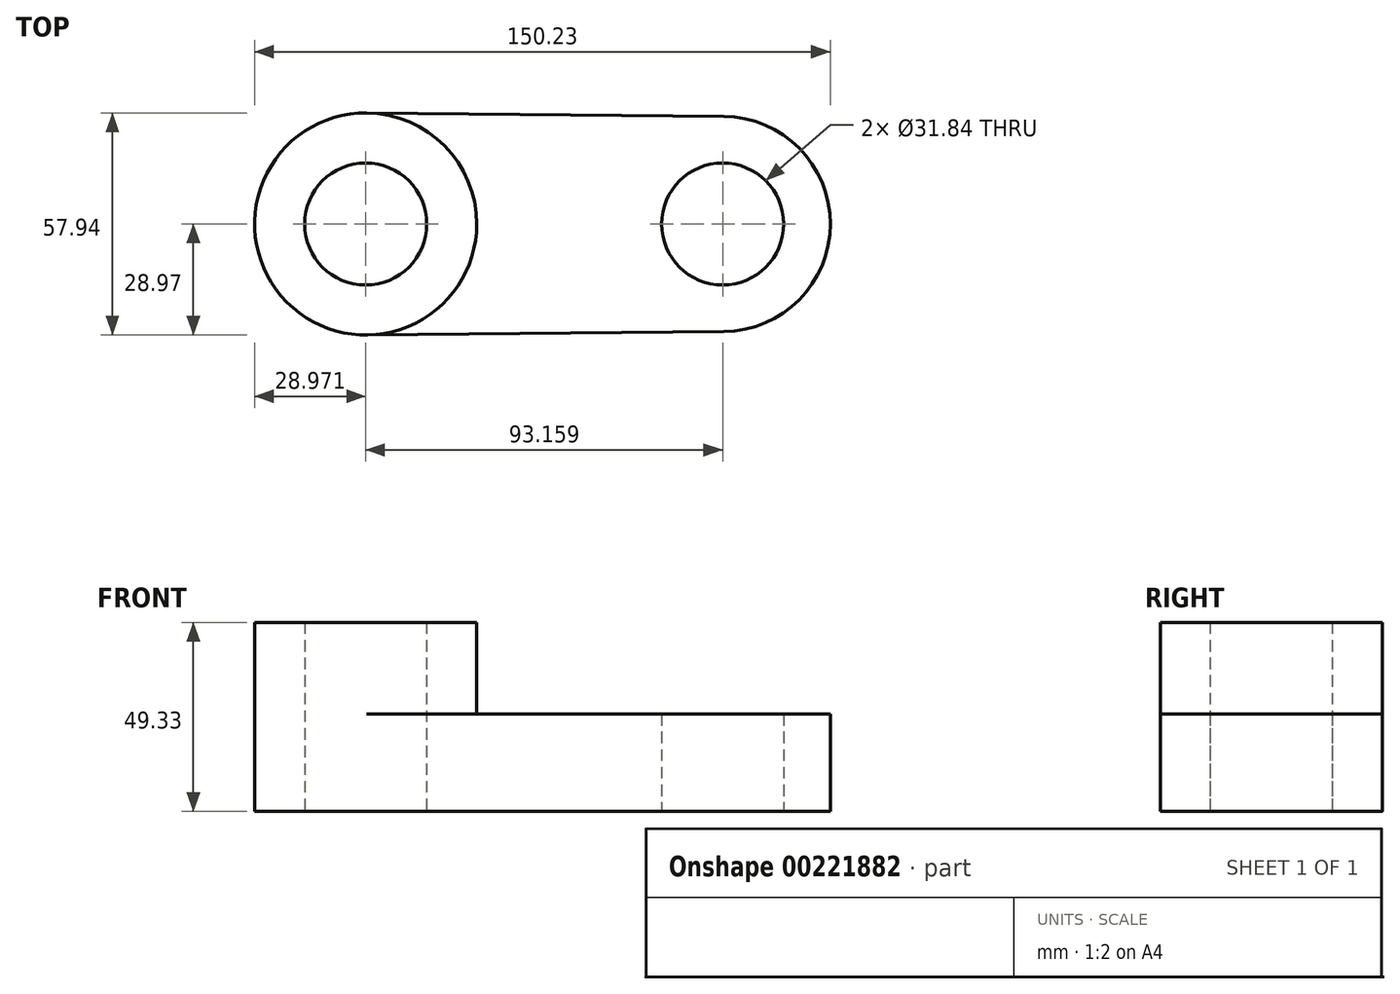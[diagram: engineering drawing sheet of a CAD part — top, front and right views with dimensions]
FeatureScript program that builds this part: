
annotation { "Feature Type Name" : "Feature", "Feature Type Description" : "" }
export const myFeature = defineFeature(function(context is Context, id is Id, definition is map)
    precondition{}
    {
        {
            var Q0;
            Q0=qCreatedBy(makeId("Top.planeOp"),FACE);
            var sketch = newSketch(context, id + "F0", { "sketchPlane" : qUnion([Q0])});
            skCircle(sketch, "E0", {"center": v(-46.58, 0) * mm, "radius": 15.92 * mm});
            skCircle(sketch, "E1", {"center": v(46.58, 0) * mm, "radius": 15.92 * mm});
            skArc(sketch, "E2", {"start": v(-46.3, 28.97) * mm, "mid": v(-75.55, 0) * mm, "end": v(-46.3, -28.97) * mm});
            skArc(sketch, "E3", {"start": v(46.84, -28.1) * mm, "mid": v(74.68, 0) * mm, "end": v(46.84, 28.1) * mm});
            skLineSegment(sketch, "E4", {"start": v(-46.3, 28.97) * mm, "end": v(46.84, 28.1) * mm});
            skLineSegment(sketch, "E5", {"start": v(46.84, -28.1) * mm, "end": v(-46.3, -28.97) * mm});
            skArc(sketch, "E6", {"start": v(-46.3, -28.97) * mm, "mid": v(-17.6, 0) * mm, "end": v(-46.3, 28.97) * mm});
            skSolve(sketch);
        }
        {
            var Q0;
            Q0 = qSketchRegion(id + "F0", true);
            extrude(context, id + "F1", {"entities" : qUnion([Q0]), "depth" : 25.4 * mm});
        }
        {
            var Q0;
            Q0=makeQuery(id+"F0.imprint","IMPRINT",FACE,{"disambiguationData":[TD([[makeQuery(id+"F0.imprint","IMPRINT",EDGE,{"derivedFrom":sQuery(id+"F0.wireOp",EDGE,"E0")}),-1.0]])]});
            extrude(context, id + "F2", {"entities" : qUnion([Q0]), "operationType" : NewBodyOperationType.ADD, "depth" : 49.33 * mm});
        }
    });
